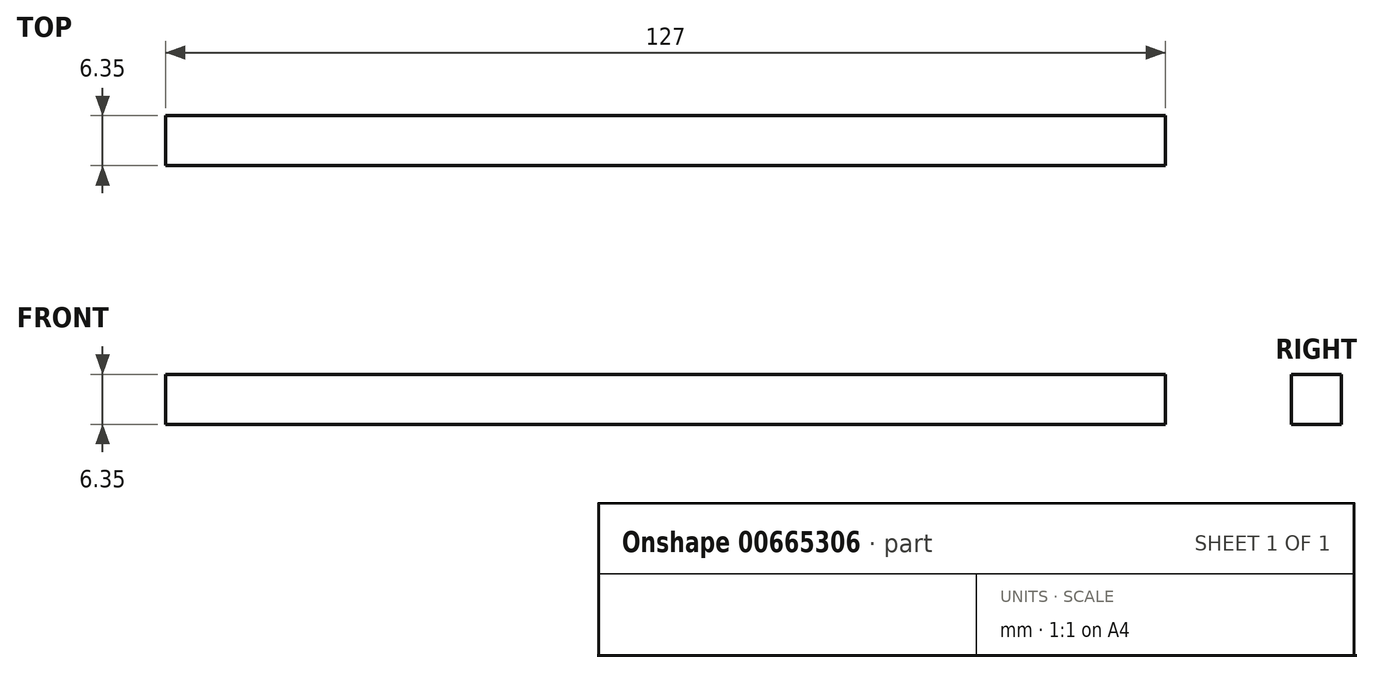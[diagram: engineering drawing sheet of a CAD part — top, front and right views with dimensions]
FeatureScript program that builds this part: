
annotation { "Feature Type Name" : "Feature", "Feature Type Description" : "" }
export const myFeature = defineFeature(function(context is Context, id is Id, definition is map)
    precondition{}
    {
        {
            var Q0;
            Q0=qCreatedBy(makeId("Top.planeOp"),FACE);
            var sketch = newSketch(context, id + "F0", { "sketchPlane" : qUnion([Q0])});
            skLineSegment(sketch, "E0.bottom", {"start": v(0, 0) * mm, "end": v(127, 0) * mm});
            skLineSegment(sketch, "E0.top", {"start": v(0, -6.35) * mm, "end": v(127, -6.35) * mm});
            skLineSegment(sketch, "E0.left", {"start": v(0, 0) * mm, "end": v(0, -6.35) * mm});
            skLineSegment(sketch, "E0.right", {"start": v(127, 0) * mm, "end": v(127, -6.35) * mm});
            skSolve(sketch);
        }
        {
            var Q0;
            Q0=makeQuery(id+"F0.imprint","IMPRINT",FACE,{"disambiguationData":[TD([[makeQuery(id+"F0.imprint","IMPRINT",EDGE,{"derivedFrom":sQuery(id+"F0.wireOp",EDGE,"E0.bottom")}),-1.0]])]});
            extrude(context, id + "F1", {"entities" : qUnion([Q0]), "depth" : 6.35 * mm, "offsetDistance" : 25.4 * mm});
        }
    });
